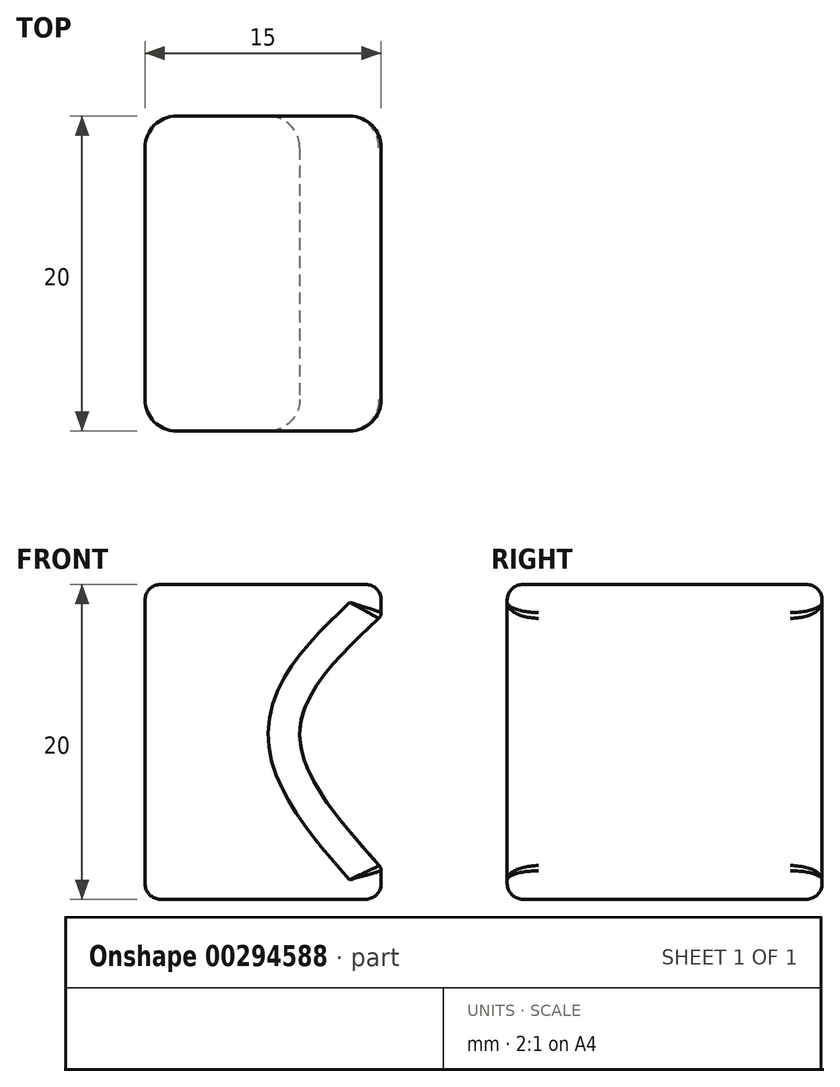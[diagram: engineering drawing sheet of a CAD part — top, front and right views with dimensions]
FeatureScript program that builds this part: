
annotation { "Feature Type Name" : "Feature", "Feature Type Description" : "" }
export const myFeature = defineFeature(function(context is Context, id is Id, definition is map)
    precondition{}
    {
        {
            var Q0;
            Q0=qCreatedBy(makeId("Front.planeOp"),FACE);
            var sketch = newSketch(context, id + "F0", { "sketchPlane" : qUnion([Q0])});
            skLineSegment(sketch, "E0", {"start": v(-51.45, -58.09) * mm, "end": v(-36.45, -58.09) * mm});
            skLineSegment(sketch, "E1", {"start": v(-51.45, -58.09) * mm, "end": v(-51.45, -38.09) * mm});
            skLineSegment(sketch, "E2", {"start": v(-51.45, -38.09) * mm, "end": v(-36.45, -38.09) * mm});
            skLineSegment(sketch, "E3", {"start": v(-36.45, -38.09) * mm, "end": v(-36.45, -40.09) * mm});
            skLineSegment(sketch, "E4", {"start": v(-36.45, -58.09) * mm, "end": v(-36.45, -56.09) * mm});
            skFitSpline(sketch, "E5", {"points": [v(-36.45, -40.09) * mm, v(-41.63, -47.43) * mm, v(-36.45, -56.09) * mm], "startDerivative": vector(-15.7, -14.7) * mm, "endDerivative": vector(15.4, -17.27) * mm});
            skSolve(sketch);
        }
        {
            var Q0;
            Q0 = qSketchRegion(id + "F0", true);
            extrude(context, id + "F1", {"entities" : qUnion([Q0]), "depth" : 20 * mm});
        }
        {
            var Q0;
            Q0=makeQuery(id+"F1.opExtrude","SWEPT_FACE",FACE,{"disambiguationData":[OSD([sQuery(id+"F0.wireOp",EDGE,"E2")])]});
            var Q1;
            Q1=makeQuery(id+"F1.opExtrude","CAP_EDGE",EDGE,{"disambiguationData":[OSD([sQuery(id+"F0.wireOp",EDGE,"E0")])],"isStart":false});
            var Q2;
            Q2=makeQuery(id+"F1.opExtrude","SWEPT_EDGE",EDGE,{"disambiguationData":[OSD([sQuery(id+"F0.wireOp",EDGE,"E0"),sQuery(id+"F0.wireOp",EDGE,"E1")])]});
            var Q3;
            Q3=makeQuery(id+"F1.opExtrude","SWEPT_FACE",FACE,{"disambiguationData":[OSD([sQuery(id+"F0.wireOp",EDGE,"E0")])]});
            fillet(context, id + "F2", {"entities" : qUnion([Q0, Q1, Q2, Q3]), "radius" : 1 * mm, "tangentPropagation" : true, "allowEdgeOverflow" : false});
        }
        {
            var Q0;
            Q0=makeQuery(id+"F1.opExtrude","SWEPT_EDGE",EDGE,{"disambiguationData":[OSD([sQuery(id+"F0.wireOp",EDGE,"E3"),sQuery(id+"F0.wireOp",EDGE,"E5")])]});
            var Q1;
            Q1=makeQuery(id+"F1.opExtrude","SWEPT_EDGE",EDGE,{"disambiguationData":[OSD([sQuery(id+"F0.wireOp",EDGE,"E4"),sQuery(id+"F0.wireOp",EDGE,"E5")])]});
            fillet(context, id + "F3", {"entities" : qUnion([Q0, Q1]), "radius" : 0.5 * mm, "tangentPropagation" : true, "allowEdgeOverflow" : false});
        }
        {
            var Q0;
            {var subQ0=sQuery(id+"F0.wireOp",EDGE,"E2");Q0=makeQuery(id+"F2.opFillet","BLEND_EDGE",EDGE,{"blendedFrom":[makeQuery(id+"F1.opExtrude","SWEPT_EDGE",EDGE,{"disambiguationData":[OSD([sQuery(id+"F0.wireOp",EDGE,"E1"),subQ0])]}),makeQuery(id+"F1.opExtrude","CAP_EDGE",EDGE,{"disambiguationData":[OSD([subQ0])],"isStart":false})],"blendedInto":[]});}
            var Q1;
            {var subQ0=sQuery(id+"F0.wireOp",EDGE,"E2");Q1=makeQuery(id+"F2.opFillet","BLEND_EDGE",EDGE,{"blendedFrom":[makeQuery(id+"F1.opExtrude","SWEPT_EDGE",EDGE,{"disambiguationData":[OSD([sQuery(id+"F0.wireOp",EDGE,"E1"),subQ0])]}),makeQuery(id+"F1.opExtrude","CAP_EDGE",EDGE,{"disambiguationData":[OSD([subQ0])],"isStart":true})],"blendedInto":[]});}
            var Q2;
            {var subQ0=sQuery(id+"F0.wireOp",EDGE,"E2");Q2=makeQuery(id+"F2.opFillet","BLEND_EDGE",EDGE,{"blendedFrom":[makeQuery(id+"F1.opExtrude","SWEPT_EDGE",EDGE,{"disambiguationData":[OSD([subQ0,sQuery(id+"F0.wireOp",EDGE,"E3")])]}),makeQuery(id+"F1.opExtrude","CAP_EDGE",EDGE,{"disambiguationData":[OSD([subQ0])],"isStart":false})],"blendedInto":[]});}
            var Q3;
            {var subQ0=sQuery(id+"F0.wireOp",EDGE,"E2");Q3=makeQuery(id+"F2.opFillet","BLEND_EDGE",EDGE,{"blendedFrom":[makeQuery(id+"F1.opExtrude","SWEPT_EDGE",EDGE,{"disambiguationData":[OSD([subQ0,sQuery(id+"F0.wireOp",EDGE,"E3")])]}),makeQuery(id+"F1.opExtrude","CAP_EDGE",EDGE,{"disambiguationData":[OSD([subQ0])],"isStart":true})],"blendedInto":[]});}
            fillet(context, id + "F4", {"entities" : qUnion([Q0, Q1, Q2, Q3]), "radius" : 2 * mm, "tangentPropagation" : true, "allowEdgeOverflow" : false});
        }
    });
